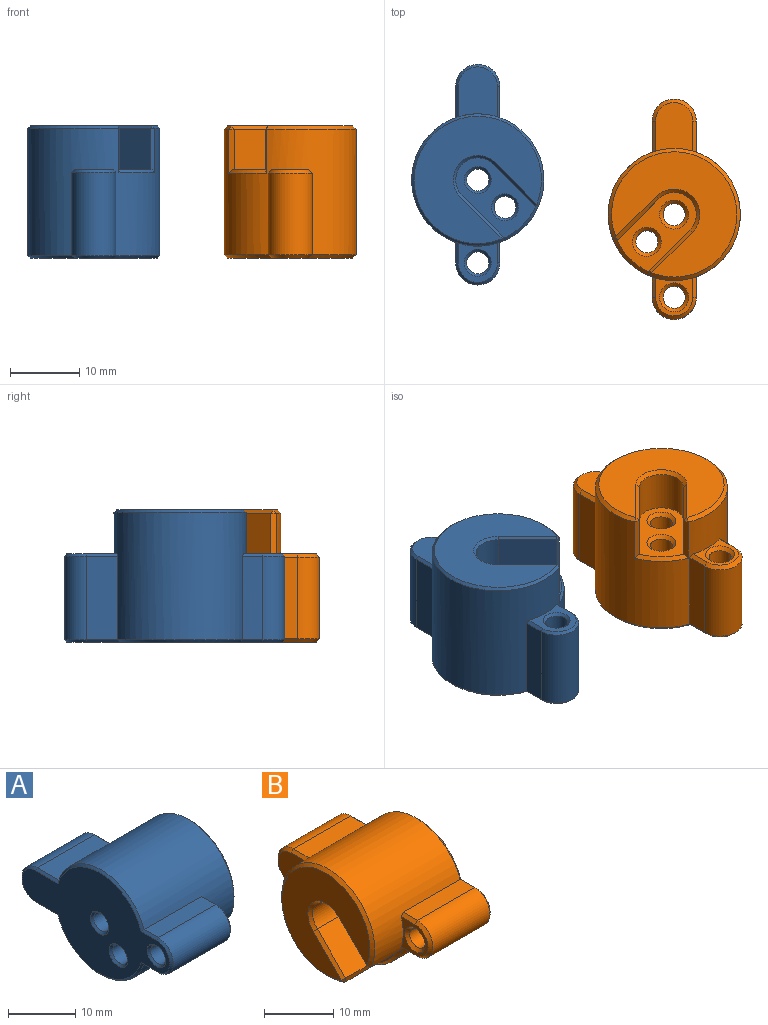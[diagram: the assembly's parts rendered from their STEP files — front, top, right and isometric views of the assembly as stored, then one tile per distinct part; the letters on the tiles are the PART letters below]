
ASSEMBLY  parts=2 mates=1
PART A: 47 faces, bbox 19.1x31.8x19.1 mm
  f0: plane 7.19x5.64mm, normal (1,0,0), area 35.6mm2, adj f5,f29,f30,f31
  f1: plane 5.65x5.64mm, normal (1,0,0), area 15mm2, adj f5,f26,f27,f28,f46
  f2: plane 11.99x4.49mm, normal (0,0,-1), area 53.8mm2, adj f3,f5,f18,f29
  f3: cylinder r=3.17mm len=11.99mm, axis (1,0,0), area 119.6mm2, adj f2,f4,f19,f30
  f4: plane 11.99x4.49mm, normal (0,0,1), area 53.8mm2, adj f3,f5,f21,f31
  f5: cylinder r=9.53mm len=19.05mm, axis (1,0,0), area 890.4mm2, adj f0,f1,f2,f4,f6,f10,f20,f23
  f6: plane 11.99x2.95mm, normal (0,0,1), area 35.4mm2, adj f5,f7,f25,f28
  f7: cylinder r=3.17mm len=11.99mm, axis (1,0,0), area 119.6mm2, adj f6,f10,f24,f27
  f8: cylinder r=1.59mm len=11.99mm, axis (1,0,0), area 119.6mm2, adj f41,f42
  f9: cylinder r=1.59mm len=11.99mm, axis (1,0,0), area 119.6mm2, adj f44,f45
  f10: plane 11.99x2.95mm, normal (0,0,-1), area 35.4mm2, adj f5,f7,f22,f26
  f11: cylinder r=1.59mm len=11.99mm, axis (1,0,0), area 119.6mm2, adj f43,f46
  f12: plane 31.04x18.34mm, normal (-1,0,0), area 295.2mm2, adj f18,f19,f20,f21,f22,f23,f24,f25
  f13: plane 11.56x11.56mm, normal (1,0,0), area 49.2mm2, adj f14,f15,f16,f32,f34,f37,f42,f45
  f14: plane 6x5.99mm, normal (0,0.71,-0.71), area 50.8mm2, adj f13,f15,f32,f35
  f15: cylinder r=3.17mm len=6mm, axis (-1,0,0), area 59.8mm2, adj f13,f14,f16,f38
  f16: plane 6x5.99mm, normal (0,-0.71,0.71), area 50.8mm2, adj f13,f15,f37,f40
  f17: plane 18.34x18.34mm, normal (1,0,0), area 181.6mm2, adj f35,f36,f38,f40
  f18: plane 4.75x0.36mm, normal (-0.71,0,-0.71), area 2.3mm2, adj f2,f12,f19,f20
  f19: cone r=3.17mm half-angle=45deg, axis (1,0,0), area 4.7mm2, adj f3,f12,f18,f21
  f20: cone r=9.53mm half-angle=45deg, axis (1,0,0), area 11.6mm2, adj f5,f12,f18,f22
  f21: plane 4.75x0.36mm, normal (-0.71,0,0.71), area 2.3mm2, adj f4,f12,f19,f23
  f22: plane 3.21x0.36mm, normal (-0.71,0,-0.71), area 1.5mm2, adj f10,f12,f20,f24
  f23: cone r=9.53mm half-angle=45deg, axis (1,0,0), area 11.6mm2, adj f5,f12,f21,f25
  f24: cone r=3.17mm half-angle=45deg, axis (1,0,0), area 4.7mm2, adj f7,f12,f22,f25
  f25: plane 3.21x0.36mm, normal (-0.71,0,0.71), area 1.5mm2, adj f6,f12,f23,f24
  f26: plane 2.95x0.35mm, normal (0.71,0,-0.71), area 1.4mm2, adj f1,f5,f10,f27
  f27: cone r=2.82mm half-angle=45deg, axis (-1,0,0), area 4.7mm2, adj f1,f7,f26,f28
  f28: plane 2.95x0.35mm, normal (0.71,0,0.71), area 1.4mm2, adj f1,f5,f6,f27
  f29: plane 4.49x0.35mm, normal (0.71,0,-0.71), area 2.2mm2, adj f0,f2,f5,f30
  f30: cone r=2.82mm half-angle=45deg, axis (-1,0,0), area 4.7mm2, adj f0,f3,f29,f31
  f31: plane 4.49x0.35mm, normal (0.71,0,0.71), area 2.2mm2, adj f0,f4,f5,f30
  f32: plane 6.36x0.58mm, normal (0,-0.2,-0.98), area 3.6mm2, adj f5,f13,f14,f33,f34
  f33: plane 0.58x0.35mm, normal (0.49,-0.17,-0.86), area 0.1mm2, adj f32,f35,f36
  f34: cone r=9.17mm half-angle=45deg, axis (-1,0,0), area 3.6mm2, adj f5,f13,f32,f37
  f35: plane 6.24x6.24mm, normal (0.71,0.5,-0.5), area 4.2mm2, adj f14,f17,f33,f38
  f36: cone r=9.17mm half-angle=45deg, axis (-1,0,0), area 25.7mm2, adj f5,f17,f33,f39
  f37: plane 6.36x0.58mm, normal (0,-0.98,-0.2), area 3.6mm2, adj f5,f13,f16,f34,f39
  f38: cone r=3.17mm half-angle=45deg, axis (1,0,0), area 5.3mm2, adj f15,f17,f35,f40
  f39: plane 0.58x0.35mm, normal (0.49,-0.86,-0.17), area 0.1mm2, adj f36,f37,f40
  f40: plane 6.24x6.24mm, normal (0.71,-0.5,0.5), area 4.2mm2, adj f16,f17,f38,f39
  f41: cone r=1.94mm half-angle=45deg, axis (-1,0,0), area 5.5mm2, adj f8,f12
  f42: cone r=1.59mm half-angle=45deg, axis (1,0,0), area 5.5mm2, adj f8,f13
  f43: cone r=1.94mm half-angle=45deg, axis (-1,0,0), area 5.5mm2, adj f11,f12
  f44: cone r=1.94mm half-angle=45deg, axis (-1,0,0), area 5.5mm2, adj f9,f12
  f45: cone r=1.59mm half-angle=45deg, axis (1,0,0), area 5.5mm2, adj f9,f13
  f46: cone r=1.59mm half-angle=45deg, axis (1,0,0), area 5.5mm2, adj f1,f11
PART B: 47 faces, bbox 19.1x31.8x19.1 mm
  f0: plane 7x5.35mm, normal (-1,0,0), area 33mm2, adj f5,f26,f27,f28
  f1: plane 5.46x5.35mm, normal (-1,0,0), area 11.1mm2, adj f5,f29,f30,f31,f33
  f2: plane 11.7x2.95mm, normal (0,0,-1), area 34.5mm2, adj f3,f5,f18,f29
  f3: cylinder r=3.17mm len=11.7mm, axis (-1,0,0), area 116.7mm2, adj f2,f4,f20,f30
  f4: plane 11.7x2.95mm, normal (0,0,1), area 34.5mm2, adj f3,f5,f22,f31
  f5: cylinder r=9.53mm len=19.05mm, axis (-1,0,0), area 872.1mm2, adj f0,f1,f2,f4,f6,f10,f19,f24
  f6: plane 11.7x4.49mm, normal (0,0,1), area 52.5mm2, adj f5,f7,f25,f28
  f7: cylinder r=3.17mm len=11.7mm, axis (-1,0,0), area 116.7mm2, adj f6,f10,f23,f27
  f8: cylinder r=1.59mm len=11.7mm, axis (-1,0,0), area 116.7mm2, adj f36,f37
  f9: cylinder r=1.59mm len=11.7mm, axis (-1,0,0), area 116.7mm2, adj f32,f33
  f10: plane 11.7x4.49mm, normal (0,0,-1), area 52.5mm2, adj f5,f7,f21,f26
  f11: cylinder r=1.59mm len=11.7mm, axis (-1,0,0), area 116.7mm2, adj f34,f35
  f12: plane 30.75x18.05mm, normal (1,0,0), area 278.1mm2, adj f18,f19,f20,f21,f22,f23,f24,f25
  f13: plane 11.48x11.48mm, normal (-1,0,0), area 44.6mm2, adj f14,f15,f16,f35,f37,f43,f45,f46
  f14: plane 5.85x5.83mm, normal (0,-0.71,0.71), area 48.2mm2, adj f13,f15,f42,f46
  f15: cylinder r=3.17mm len=5.85mm, axis (1,0,0), area 58.4mm2, adj f13,f14,f16,f39
  f16: plane 5.85x5.83mm, normal (0,0.71,-0.71), area 48.2mm2, adj f13,f15,f38,f43
  f17: plane 18.05x18.05mm, normal (-1,0,0), area 170.2mm2, adj f38,f39,f41,f42
  f18: plane 3.32x0.51mm, normal (0.71,0,-0.71), area 2.2mm2, adj f2,f12,f19,f20
  f19: cone r=9.03mm half-angle=45deg, axis (-1,0,0), area 16.4mm2, adj f5,f12,f18,f21
  f20: cone r=2.67mm half-angle=45deg, axis (-1,0,0), area 6.5mm2, adj f3,f12,f18,f22
  f21: plane 4.86x0.51mm, normal (0.71,0,-0.71), area 3.3mm2, adj f10,f12,f19,f23
  f22: plane 3.32x0.51mm, normal (0.71,0,0.71), area 2.2mm2, adj f4,f12,f20,f24
  f23: cone r=2.67mm half-angle=45deg, axis (-1,0,0), area 6.5mm2, adj f7,f12,f21,f25
  f24: cone r=9.03mm half-angle=45deg, axis (-1,0,0), area 16.4mm2, adj f5,f12,f22,f25
  f25: plane 4.86x0.51mm, normal (0.71,0,0.71), area 3.3mm2, adj f6,f12,f23,f24
  f26: plane 4.49x0.5mm, normal (-0.71,0,-0.71), area 3.1mm2, adj f0,f5,f10,f27
  f27: cone r=3.17mm half-angle=45deg, axis (1,0,0), area 6.5mm2, adj f0,f7,f26,f28
  f28: plane 4.49x0.5mm, normal (-0.71,0,0.71), area 3.1mm2, adj f0,f5,f6,f27
  f29: plane 2.95x0.5mm, normal (-0.71,0,-0.71), area 2mm2, adj f1,f2,f5,f30
  f30: cone r=3.17mm half-angle=45deg, axis (1,0,0), area 6.5mm2, adj f1,f3,f29,f31
  f31: plane 2.95x0.5mm, normal (-0.71,0,0.71), area 2mm2, adj f1,f4,f5,f30
  f32: cone r=1.59mm half-angle=45deg, axis (1,0,0), area 8.2mm2, adj f9,f12
  f33: cone r=2.09mm half-angle=45deg, axis (-1,0,0), area 8.2mm2, adj f1,f9
  f34: cone r=1.59mm half-angle=45deg, axis (1,0,0), area 8.2mm2, adj f11,f12
  f35: cone r=2.09mm half-angle=45deg, axis (-1,0,0), area 8.2mm2, adj f11,f13
  f36: cone r=1.59mm half-angle=45deg, axis (1,0,0), area 8.2mm2, adj f8,f12
  f37: cone r=2.09mm half-angle=45deg, axis (-1,0,0), area 8.2mm2, adj f8,f13
  f38: plane 6.18x6.18mm, normal (-0.71,0.5,-0.5), area 5.8mm2, adj f16,f17,f39,f40
  f39: cone r=3.67mm half-angle=45deg, axis (-1,0,0), area 7.6mm2, adj f15,f17,f38,f42
  f40: plane 0.82x0.5mm, normal (-0.48,-0.18,-0.86), area 0.2mm2, adj f38,f41,f43
  f41: cone r=9.53mm half-angle=45deg, axis (1,0,0), area 35.7mm2, adj f5,f17,f40,f44
  f42: plane 6.18x6.18mm, normal (-0.71,-0.5,0.5), area 5.8mm2, adj f14,f17,f39,f44
  f43: plane 6.36x0.83mm, normal (0,-0.21,-0.98), area 5.1mm2, adj f5,f13,f16,f40,f45
  f44: plane 0.82x0.5mm, normal (-0.48,-0.86,-0.18), area 0.2mm2, adj f41,f42,f46
  f45: cone r=9.53mm half-angle=45deg, axis (1,0,0), area 5.3mm2, adj f5,f13,f43,f46
  f46: plane 6.36x0.83mm, normal (0,-0.98,-0.21), area 5.1mm2, adj f5,f13,f14,f44,f45
PLACE A rot(axis=(0,-1,0),90deg) t=(8.79,-24.33,-273.16)mm
PLACE B rot(axis=(0,1,0),90deg) t=(30.35,-29.31,-273.16)mm
MATE planar B.f8 <-> A.f12  axis (0,0,-1) through (29.79,-11.91,-31.86)mm
